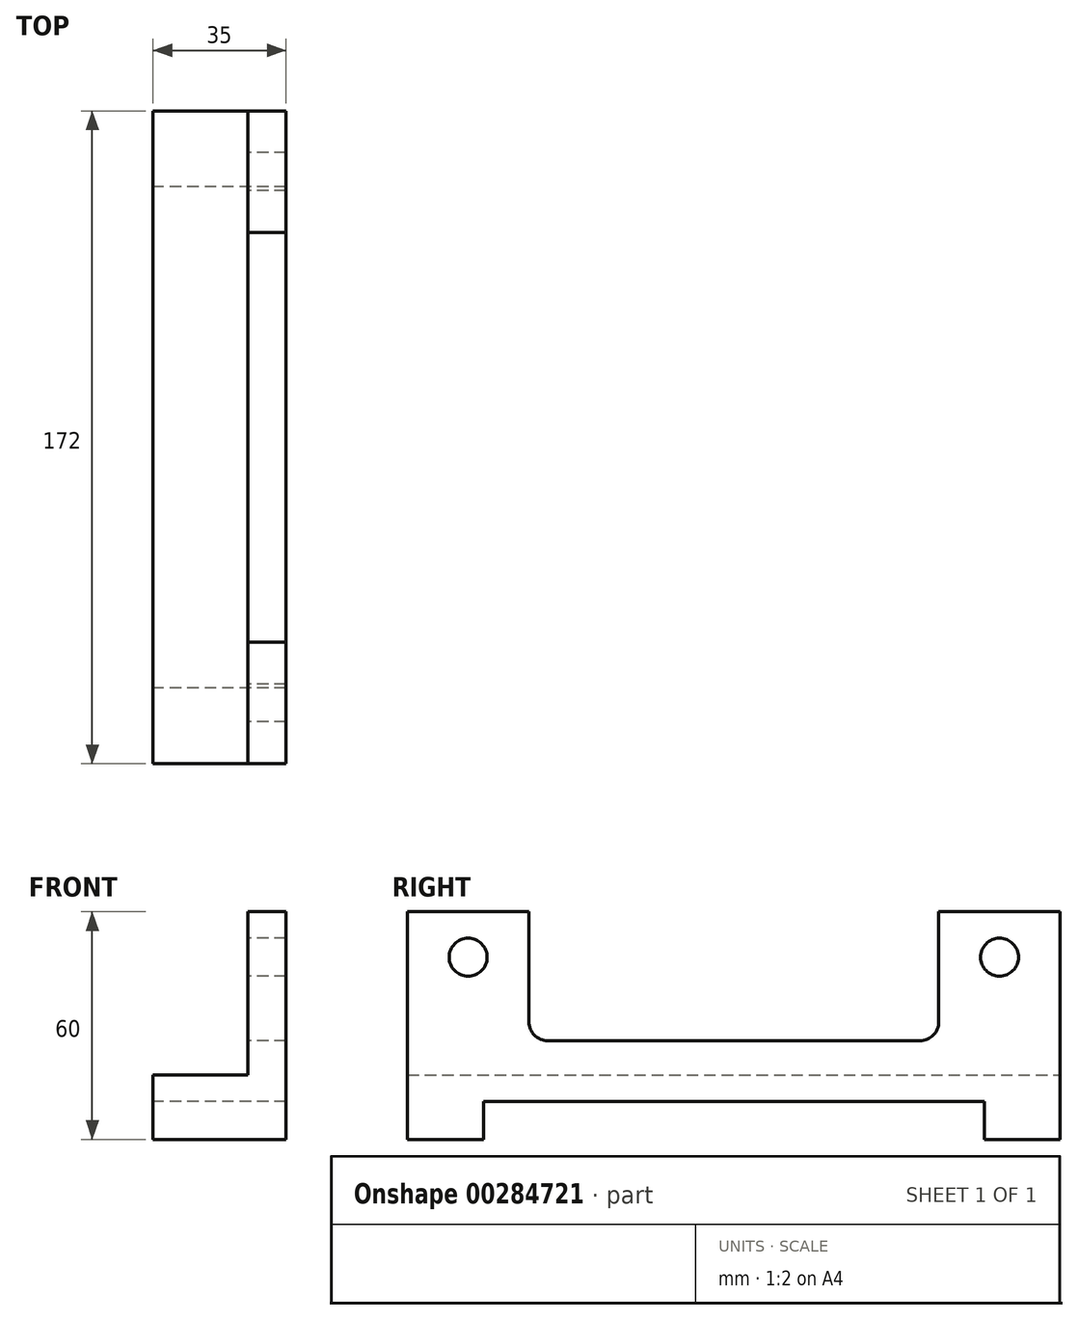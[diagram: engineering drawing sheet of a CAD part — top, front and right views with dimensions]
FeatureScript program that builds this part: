
annotation { "Feature Type Name" : "Feature", "Feature Type Description" : "" }
export const myFeature = defineFeature(function(context is Context, id is Id, definition is map)
    precondition{}
    {
        {
            var Q0;
            Q0=qCreatedBy(makeId("Front.planeOp"),FACE);
            var sketch = newSketch(context, id + "F0", { "sketchPlane" : qUnion([Q0])});
            skLineSegment(sketch, "E0.bottom", {"start": v(0, 0) * mm, "end": v(10, 0) * mm});
            skLineSegment(sketch, "E0.top", {"start": v(0, 60) * mm, "end": v(10, 60) * mm});
            skLineSegment(sketch, "E0.left", {"start": v(0, 17) * mm, "end": v(0, 60) * mm});
            skLineSegment(sketch, "E0.right", {"start": v(10, 0) * mm, "end": v(10, 60) * mm});
            skLineSegment(sketch, "E1.bottom", {"start": v(10, 0) * mm, "end": v(-25, 0) * mm});
            skLineSegment(sketch, "E1.top", {"start": v(0, 17) * mm, "end": v(-25, 17) * mm});
            skLineSegment(sketch, "E1.left", {"start": v(10, 0) * mm, "end": v(10, 17) * mm});
            skLineSegment(sketch, "E1.right", {"start": v(-25, 0) * mm, "end": v(-25, 17) * mm});
            skSolve(sketch);
        }
        {
            var Q0;
            Q0=qSketchRegion(id+"F0",true);
            extrude(context, id + "F1", {"entities" : qUnion([Q0]), "depth" : 172 * mm});
        }
        {
            var Q0;
            Q0=makeQuery(id+"F1.opExtrude","SWEPT_FACE",FACE,{"disambiguationData":[OSD([sQuery(id+"F0.wireOp",EDGE,"E0.left")])]});
            var sketch = newSketch(context, id + "F2", { "sketchPlane" : qUnion([Q0])});
            skLineSegment(sketch, "E2", {"start": v(140, 60) * mm, "end": v(140, 31) * mm});
            skLineSegment(sketch, "E3", {"start": v(32, 60) * mm, "end": v(32, 31) * mm});
            skLineSegment(sketch, "E4", {"start": v(37, 26) * mm, "end": v(135, 26) * mm});
            skLineSegment(sketch, "E5", {"start": v(32, 60) * mm, "end": v(140, 60) * mm});
            skPoint(sketch, "E6.visualSharp", {"position": v(32, 26) * mm});
            skArc(sketch, "E6.filletArc", {"start": v(32, 31) * mm, "mid": v(33.46, 27.46) * mm, "end": v(37, 26) * mm});
            skPoint(sketch, "E7.visualSharp", {"position": v(140, 26) * mm});
            skArc(sketch, "E7.filletArc", {"start": v(135, 26) * mm, "mid": v(138.54, 27.46) * mm, "end": v(140, 31) * mm});
            skSolve(sketch);
        }
        {
            var Q0;
            Q0=qSketchRegion(id+"F2",true);
            extrude(context, id + "F3", {"entities" : qUnion([Q0]), "operationType" : NewBodyOperationType.REMOVE, "oppositeDirection" : true, "depth" : 10 * mm});
        }
        {
            var Q0;
            Q0=qCreatedBy(makeId("Right.planeOp"),FACE);
            cPlane(context, id + "F4", {"entities" : qUnion([Q0]), "cplaneType" : CPlaneType.OFFSET, "offset" : 25 * mm, "oppositeDirection" : true, "width" : 150 * mm, "height" : 150 * mm});
        }
        {
            var Q0;
            Q0=qCreatedBy(id+"F4.planeOp",FACE);
            var sketch = newSketch(context, id + "F5", { "sketchPlane" : qUnion([Q0])});
            skLineSegment(sketch, "E8", {"start": v(-20, 0) * mm, "end": v(-20, 10) * mm});
            skLineSegment(sketch, "E9", {"start": v(-152, 0) * mm, "end": v(-152, 10) * mm});
            skLineSegment(sketch, "E10", {"start": v(-152, 10) * mm, "end": v(-20, 10) * mm});
            skLineSegment(sketch, "E11", {"start": v(-152, 0) * mm, "end": v(-20, 0) * mm});
            skPoint(sketch, "E12.0.end.orphan", {"position": v(0, 17) * mm});
            skPoint(sketch, "E13.start.orphan", {"position": v(0, 0) * mm});
            skPoint(sketch, "E14.0.end.orphan", {"position": v(-172, 17) * mm});
            skPoint(sketch, "E14.0.start.orphan", {"position": v(-172, 0) * mm});
            skSolve(sketch);
        }
        {
            var Q0;
            Q0=qSketchRegion(id+"F5",true);
            extrude(context, id + "F6", {"entities" : qUnion([Q0]), "operationType" : NewBodyOperationType.REMOVE, "depth" : 35 * mm});
        }
        {
            var Q0;
            Q0=makeQuery(id+"F1.opExtrude","SWEPT_FACE",FACE,{"disambiguationData":[OSD([sQuery(id+"F0.wireOp",EDGE,"E0.left")])]});
            var sketch = newSketch(context, id + "F7", { "sketchPlane" : qUnion([Q0])});
            skPoint(sketch, "E15", {"position": v(16, 48) * mm});
            skPoint(sketch, "E16", {"position": v(156, 48) * mm});
            skSolve(sketch);
        }
        {
            var Q0;
            Q0=sQuery(id+"F7.wireOp",VERTEX,"E15");
            var Q1;
            Q1=sQuery(id+"F7.wireOp",VERTEX,"E16");
            var Q2;
            Q2=makeQuery(id+"F1.opExtrude","SWEPT_BODY",BODY,{"disambiguationData":[OSD([sQuery(id+"F0.wireOp",EDGE,"E0.top"),sQuery(id+"F0.wireOp",EDGE,"E0.left"),sQuery(id+"F0.wireOp",EDGE,"E0.right"),sQuery(id+"F0.wireOp",EDGE,"E1.bottom"),sQuery(id+"F0.wireOp",EDGE,"E1.top"),sQuery(id+"F0.wireOp",EDGE,"E1.left"),sQuery(id+"F0.wireOp",EDGE,"E1.right")])]});
            hole(context, id + "F8", {"style" : HoleStyle.SIMPLE, "endStyle" : HoleEndStyle.THROUGH, "holeDiameter" : 10 * mm, "locations" : qUnion([Q0, Q1]), "scope" : qUnion([Q2]), "isTappedThrough" : true});
        }
    });
